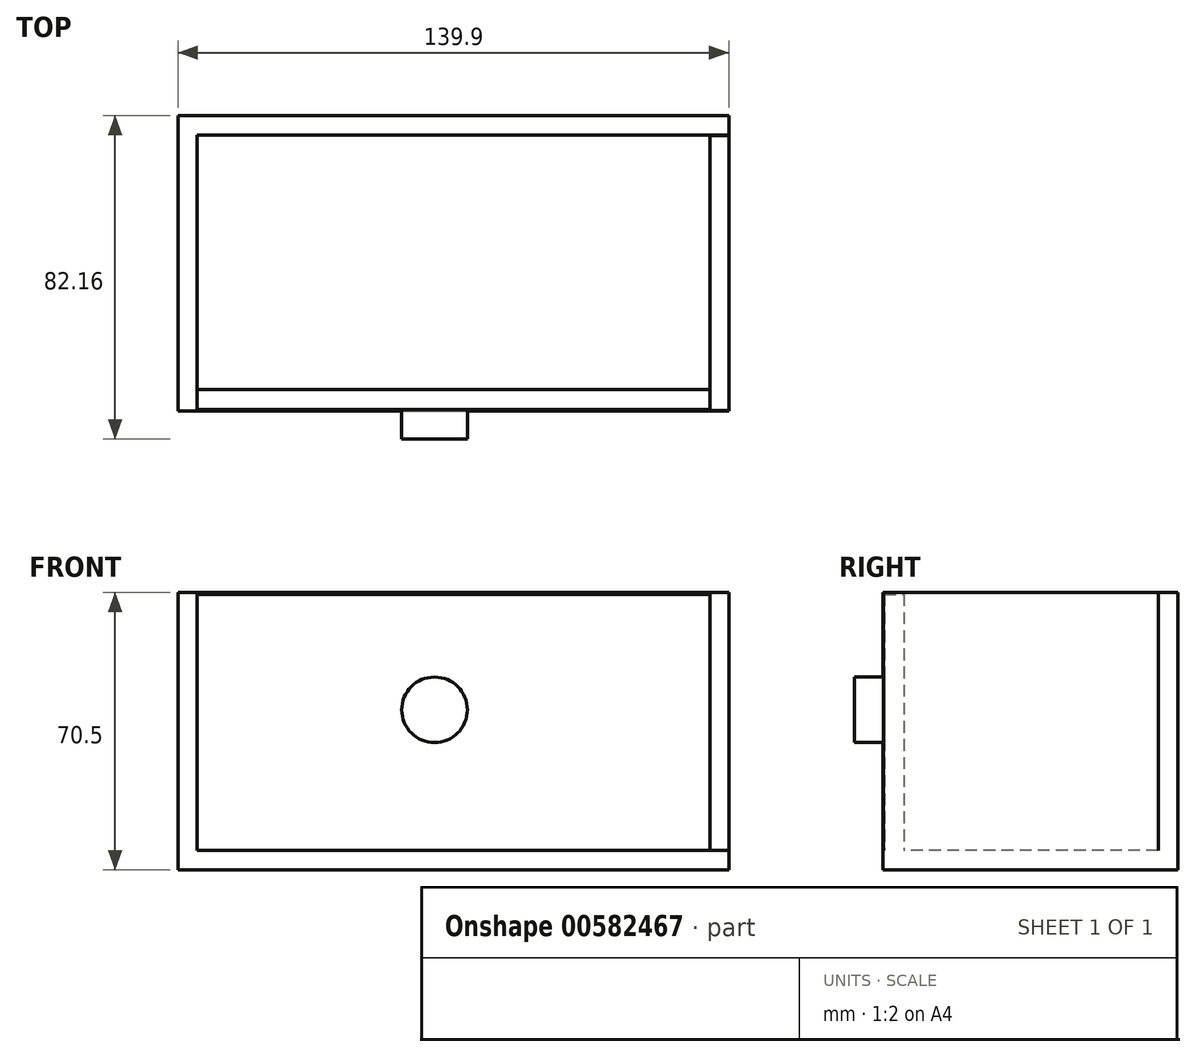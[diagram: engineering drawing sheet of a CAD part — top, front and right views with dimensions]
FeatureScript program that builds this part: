
annotation { "Feature Type Name" : "Feature", "Feature Type Description" : "" }
export const myFeature = defineFeature(function(context is Context, id is Id, definition is map)
    precondition{}
    {
        {
            var Q0;
            Q0=qCreatedBy(makeId("Top.planeOp"),FACE);
            var sketch = newSketch(context, id + "F0", { "sketchPlane" : qUnion([Q0])});
            skLineSegment(sketch, "E0.bottom", {"start": v(-65.15, -0.18) * mm, "end": v(74.75, -0.18) * mm});
            skLineSegment(sketch, "E0.top", {"start": v(-65.15, -75.18) * mm, "end": v(74.75, -75.18) * mm});
            skLineSegment(sketch, "E0.left", {"start": v(-65.15, -0.18) * mm, "end": v(-65.15, -75.18) * mm});
            skLineSegment(sketch, "E0.right", {"start": v(74.75, -0.18) * mm, "end": v(74.75, -75.18) * mm});
            skSolve(sketch);
        }
        {
            var Q0;
            Q0=makeQuery(id+"F0.imprint","IMPRINT",FACE,{"disambiguationData":[TD([[makeQuery(id+"F0.imprint","IMPRINT",EDGE,{"derivedFrom":sQuery(id+"F0.wireOp",EDGE,"E0.bottom")}),-1.0]])]});
            extrude(context, id + "F1", {"entities" : qUnion([Q0]), "depth" : 5 * mm, "offsetDistance" : 25 * mm});
        }
        {
            var Q0;
            Q0=makeQuery(id+"F1.opExtrude","CAP_FACE",FACE,{"disambiguationData":[OSD([sQuery(id+"F0.wireOp",EDGE,"E0.bottom"),sQuery(id+"F0.wireOp",EDGE,"E0.top"),sQuery(id+"F0.wireOp",EDGE,"E0.left"),sQuery(id+"F0.wireOp",EDGE,"E0.right")])],"isStart":false});
            var sketch = newSketch(context, id + "F2", { "sketchPlane" : qUnion([Q0])});
            skLineSegment(sketch, "E1.bottom", {"start": v(-65.15, -0.18) * mm, "end": v(74.75, -0.18) * mm});
            skLineSegment(sketch, "E1.top", {"start": v(-65.15, -5.18) * mm, "end": v(74.75, -5.18) * mm});
            skLineSegment(sketch, "E1.left", {"start": v(-65.15, -0.18) * mm, "end": v(-65.15, -5.18) * mm});
            skLineSegment(sketch, "E1.right", {"start": v(74.75, -0.18) * mm, "end": v(74.75, -5.18) * mm});
            skSolve(sketch);
        }
        {
            var Q0;
            {var subQ0=sQuery(id+"F2.wireOp",EDGE,"E1.top");Q0=makeQuery(id+"F2.imprint","IMPRINT",FACE,{"disambiguationData":[TD([[makeQuery(id+"F2.imprint","IMPRINT",EDGE,{"derivedFrom":subQ0}),-1.0]])]});}
            var sketch = newSketch(context, id + "F3", { "sketchPlane" : qUnion([Q0])});
            skLineSegment(sketch, "E2.bottom", {"start": v(-65.3, -4.96) * mm, "end": v(-60.3, -4.96) * mm});
            skLineSegment(sketch, "E2.top", {"start": v(-65.3, -75.36) * mm, "end": v(-60.3, -75.36) * mm});
            skLineSegment(sketch, "E2.left", {"start": v(-65.3, -4.96) * mm, "end": v(-65.3, -75.36) * mm});
            skLineSegment(sketch, "E2.right", {"start": v(-60.3, -4.96) * mm, "end": v(-60.3, -75.36) * mm});
            skSolve(sketch);
        }
        {
            var Q0;
            {var subQ0=sQuery(id+"F2.wireOp",EDGE,"E1.top");Q0=makeQuery(id+"F2.imprint","IMPRINT",FACE,{"disambiguationData":[TD([[makeQuery(id+"F2.imprint","IMPRINT",EDGE,{"derivedFrom":subQ0}),-1.0]])]});}
            var sketch = newSketch(context, id + "F4", { "sketchPlane" : qUnion([Q0])});
            skLineSegment(sketch, "E3.bottom", {"start": v(70, -5.24) * mm, "end": v(75, -5.24) * mm});
            skLineSegment(sketch, "E3.top", {"start": v(70, -75.08) * mm, "end": v(75, -75.08) * mm});
            skLineSegment(sketch, "E3.left", {"start": v(70, -5.24) * mm, "end": v(70, -75.08) * mm});
            skLineSegment(sketch, "E3.right", {"start": v(75, -5.24) * mm, "end": v(75, -75.08) * mm});
            skSolve(sketch);
        }
        {
            var Q0;
            Q0=makeQuery(id+"F2.imprint","IMPRINT",FACE,{"disambiguationData":[TD([[makeQuery(id+"F2.imprint","IMPRINT",EDGE,{"derivedFrom":sQuery(id+"F2.wireOp",EDGE,"E1.bottom")}),-1.0]])]});
            extrude(context, id + "F5", {"entities" : qUnion([Q0]), "operationType" : NewBodyOperationType.ADD, "depth" : 65.5 * mm, "offsetDistance" : 25 * mm});
        }
        {
            var Q0;
            {var subQ0=sQuery(id+"F3.wireOp",EDGE,"E2.right");var subQ1=sQuery(id+"F2.wireOp",EDGE,"E1.top");var subQ2=makeQuery(id+"F2.imprint","IMPRINT",EDGE,{"derivedFrom":subQ1});var subQ3=makeQuery(id+"F3.imprint","INTERSECT",VERTEX,{"derivedFrom":[subQ2,subQ0]});Q0=makeQuery(id+"F3.imprint","IMPRINT",FACE,{"disambiguationData":[TD([[makeQuery(id+"F3.imprint","IMPRINT",EDGE,{"disambiguationData":[TD([[subQ3,-1.0]])],"derivedFrom":subQ0}),-1.0]])]});}
            extrude(context, id + "F6", {"entities" : qUnion([Q0]), "operationType" : NewBodyOperationType.ADD, "depth" : 65.5 * mm, "offsetDistance" : 25 * mm});
        }
        {
            var Q0;
            {var subQ0=sQuery(id+"F4.wireOp",EDGE,"E3.left");Q0=makeQuery(id+"F4.imprint","IMPRINT",FACE,{"disambiguationData":[TD([[makeQuery(id+"F4.imprint","IMPRINT",EDGE,{"derivedFrom":subQ0}),1.0]])]});}
            extrude(context, id + "F7", {"entities" : qUnion([Q0]), "operationType" : NewBodyOperationType.ADD, "depth" : 65.5 * mm, "offsetDistance" : 25 * mm});
        }
        {
            var Q0;
            Q0=makeQuery(id+"F6.opExtrude","SWEPT_FACE",FACE,{"disambiguationData":[OSD([sQuery(id+"F3.wireOp",EDGE,"E2.right")])]});
            var sketch = newSketch(context, id + "F8", { "sketchPlane" : qUnion([Q0])});
            skSolve(sketch);
        }
        {
            var Q0;
            {var subQ0=sQuery(id+"F3.wireOp",EDGE,"E2.right");Q0=makeQuery(id+"F8.imprint","IMPRINT",FACE,{"disambiguationData":[TD([[makeQuery(id+"F8.imprint","IMPRINT",EDGE,{"derivedFrom":makeQuery(id+"F6.opExtrude","CAP_EDGE",EDGE,{"disambiguationData":[OSD([subQ0])],"isStart":false})}),1.0]])]});}
            var sketch = newSketch(context, id + "F9", { "sketchPlane" : qUnion([Q0])});
            skLineSegment(sketch, "E4.bottom", {"start": v(-74.84, 70.05) * mm, "end": v(-69.84, 70.05) * mm});
            skLineSegment(sketch, "E4.top", {"start": v(-74.84, 4.55) * mm, "end": v(-69.84, 4.55) * mm});
            skLineSegment(sketch, "E4.left", {"start": v(-74.84, 70.05) * mm, "end": v(-74.84, 4.55) * mm});
            skLineSegment(sketch, "E4.right", {"start": v(-69.84, 70.05) * mm, "end": v(-69.84, 4.55) * mm});
            skSolve(sketch);
        }
        {
            var Q0;
            {var subQ0=sQuery(id+"F9.wireOp",EDGE,"E4.bottom");Q0=makeQuery(id+"F9.imprint","IMPRINT",FACE,{"disambiguationData":[TD([[makeQuery(id+"F9.imprint","IMPRINT",EDGE,{"derivedFrom":subQ0}),-1.0]])]});}
            extrude(context, id + "F10", {"entities" : qUnion([Q0]), "operationType" : NewBodyOperationType.ADD, "depth" : 132.6 * mm, "offsetDistance" : 25 * mm});
        }
        {
            var Q0;
            Q0=makeQuery(id+"F10.opExtrude","SWEPT_FACE",FACE,{"disambiguationData":[OSD([sQuery(id+"F9.wireOp",EDGE,"E4.left")])]});
            var sketch = newSketch(context, id + "F11", { "sketchPlane" : qUnion([Q0])});
            skCircle(sketch, "E5", {"center": v(0, 40.68) * mm, "radius": 8.34 * mm});
            skSolve(sketch);
        }
        {
            var Q0;
            Q0=makeQuery(id+"F11.imprint","IMPRINT",FACE,{"disambiguationData":[TD([[makeQuery(id+"F11.imprint","IMPRINT",EDGE,{"derivedFrom":sQuery(id+"F11.wireOp",EDGE,"E5")}),1.0]])]});
            extrude(context, id + "F12", {"entities" : qUnion([Q0]), "operationType" : NewBodyOperationType.ADD, "depth" : 7.5 * mm, "offsetDistance" : 25 * mm});
        }
    });
